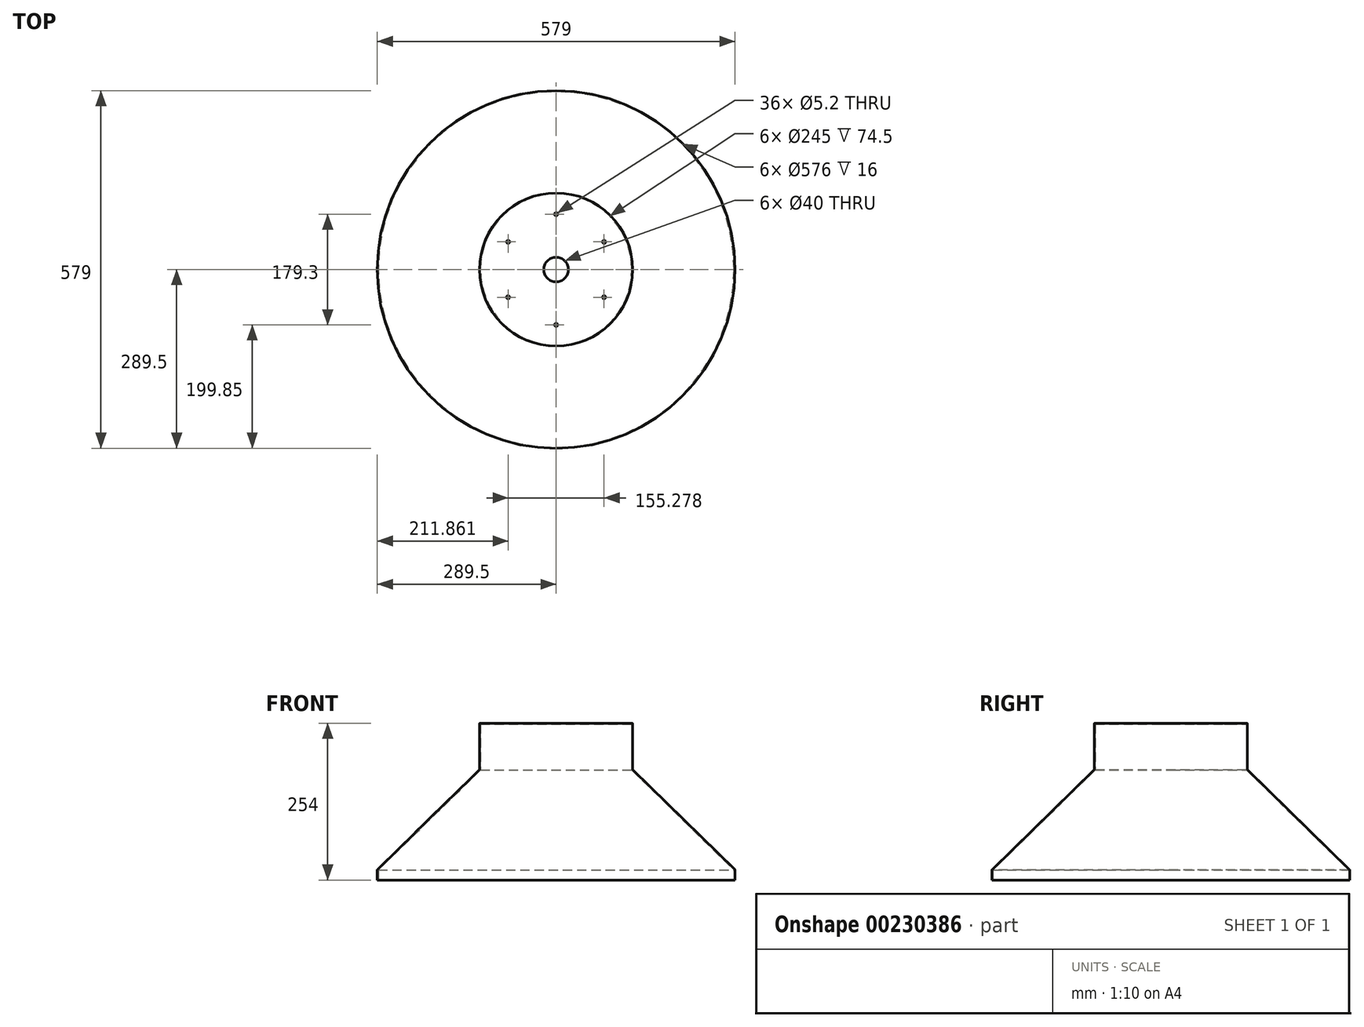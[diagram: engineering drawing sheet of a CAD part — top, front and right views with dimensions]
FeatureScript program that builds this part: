
annotation { "Feature Type Name" : "Feature", "Feature Type Description" : "" }
export const myFeature = defineFeature(function(context is Context, id is Id, definition is map)
    precondition{}
    {
        {
            var Q0;
            Q0=qCreatedBy(makeId("Front.planeOp"),FACE);
            var sketch = newSketch(context, id + "F0", { "sketchPlane" : qUnion([Q0])});
            skLineSegment(sketch, "E0", {"start": v(0, 0) * mm, "end": v(288, 0) * mm, "construction": true});
            skLineSegment(sketch, "E1", {"start": v(288, 0) * mm, "end": v(288, 16) * mm});
            skLineSegment(sketch, "E2", {"start": v(288, 16) * mm, "end": v(122.5, 178) * mm});
            skLineSegment(sketch, "E3", {"start": v(122.5, 178) * mm, "end": v(122.5, 252.5) * mm});
            skLineSegment(sketch, "E4", {"start": v(122.5, 252.5) * mm, "end": v(0, 252.5) * mm});
            skLineSegment(sketch, "E5.0", {"start": v(123, 254) * mm, "end": v(0, 254) * mm});
            skLineSegment(sketch, "E6.0", {"start": v(124, 179.05) * mm, "end": v(124, 253) * mm});
            skLineSegment(sketch, "E7.0", {"start": v(289.2, 16.92) * mm, "end": v(124.3, 178.34) * mm});
            skLineSegment(sketch, "E8.0", {"start": v(289.5, 0) * mm, "end": v(289.5, 16.21) * mm});
            skLineSegment(sketch, "E9", {"start": v(288, 0) * mm, "end": v(289.5, 0) * mm});
            skLineSegment(sketch, "E10", {"start": v(0, 254) * mm, "end": v(0, 252.5) * mm});
            skLineSegment(sketch, "E11", {"start": v(0, 0) * mm, "end": v(0, 252.5) * mm, "construction": true});
            skPoint(sketch, "E12.visualSharp", {"position": v(124, 254) * mm});
            skArc(sketch, "E12.filletArc", {"start": v(124, 253) * mm, "mid": v(123.7, 253.7) * mm, "end": v(123, 254) * mm});
            skPoint(sketch, "E13.visualSharp", {"position": v(124, 178.63) * mm});
            skArc(sketch, "E13.filletArc", {"start": v(124, 179.05) * mm, "mid": v(124.08, 178.66) * mm, "end": v(124.3, 178.34) * mm});
            skPoint(sketch, "E14.visualSharp", {"position": v(289.5, 16.63) * mm});
            skArc(sketch, "E14.filletArc", {"start": v(289.5, 16.21) * mm, "mid": v(289.42, 16.6) * mm, "end": v(289.2, 16.92) * mm});
            skSolve(sketch);
        }
        {
            var Q0;
            Q0 = qSketchRegion(id + "F0", true);
            var Q1;
            Q1=sQuery(id+"F0.wireOp",EDGE,"E11");
            revolve(context, id + "F1", {"entities" : qUnion([Q0]), "axis" : qUnion([Q1]), "revolveType" : RevolveType.FULL});
        }
        {
            var Q0;
            Q0=makeQuery(id+"F1.opRevolve","SWEPT_FACE",FACE,{"disambiguationData":[OSD([sQuery(id+"F0.wireOp",EDGE,"E5.0")])]});
            var sketch = newSketch(context, id + "F2", { "sketchPlane" : qUnion([Q0])});
            skCircle(sketch, "E15.0", {"center": v(0, 0) * mm, "radius": 123 * mm, "construction": true});
            skCircle(sketch, "E16", {"center": v(0, 0) * mm, "radius": 5 * mm});
            skSolve(sketch);
        }
        {
            var Q0;
            Q0 = qSketchRegion(id + "F2", true);
            extrude(context, id + "F3", {"entities" : qUnion([Q0]), "operationType" : NewBodyOperationType.REMOVE, "endBound" : BoundingType.UP_TO_NEXT, "oppositeDirection" : true, "depth" : 25 * mm});
        }
        {
            var Q0;
            Q0=makeQuery(id+"F1.opRevolve","SWEPT_FACE",FACE,{"disambiguationData":[OSD([sQuery(id+"F0.wireOp",EDGE,"E5.0")])]});
            var sketch = newSketch(context, id + "F4", { "sketchPlane" : qUnion([Q0])});
            skCircle(sketch, "E17", {"center": v(0, 0) * mm, "radius": 20 * mm});
            skSolve(sketch);
        }
        {
            var Q0;
            Q0 = qSketchRegion(id + "F4", true);
            extrude(context, id + "F5", {"entities" : qUnion([Q0]), "operationType" : NewBodyOperationType.REMOVE, "endBound" : BoundingType.THROUGH_ALL, "oppositeDirection" : true, "depth" : 25 * mm});
        }
        {
            var Q0;
            Q0=makeQuery(id+"F1.opRevolve","SWEPT_FACE",FACE,{"disambiguationData":[OSD([sQuery(id+"F0.wireOp",EDGE,"E5.0")])]});
            var sketch = newSketch(context, id + "F6", { "sketchPlane" : qUnion([Q0])});
            skCircle(sketch, "E18", {"center": v(0, 0) * mm, "radius": 89.65 * mm, "construction": true});
            skCircle(sketch, "E19", {"center": v(0, 89.65) * mm, "radius": 2.6 * mm});
            skCircle(sketch, "E20.1.0", {"center": v(-77.64, 44.83) * mm, "radius": 2.6 * mm});
            skCircle(sketch, "E20.2.0", {"center": v(-77.64, -44.82) * mm, "radius": 2.6 * mm});
            skCircle(sketch, "E21.1.3.0", {"center": v(0, -89.65) * mm, "radius": 2.6 * mm});
            skCircle(sketch, "E21.1.4.0", {"center": v(77.64, -44.83) * mm, "radius": 2.6 * mm});
            skCircle(sketch, "E21.1.5.0", {"center": v(77.64, 44.83) * mm, "radius": 2.6 * mm});
            skSolve(sketch);
        }
        {
            var Q0;
            Q0 = qSketchRegion(id + "F6", true);
            extrude(context, id + "F7", {"entities" : qUnion([Q0]), "operationType" : NewBodyOperationType.REMOVE, "endBound" : BoundingType.THROUGH_ALL, "oppositeDirection" : true, "depth" : 25 * mm});
        }
    });
